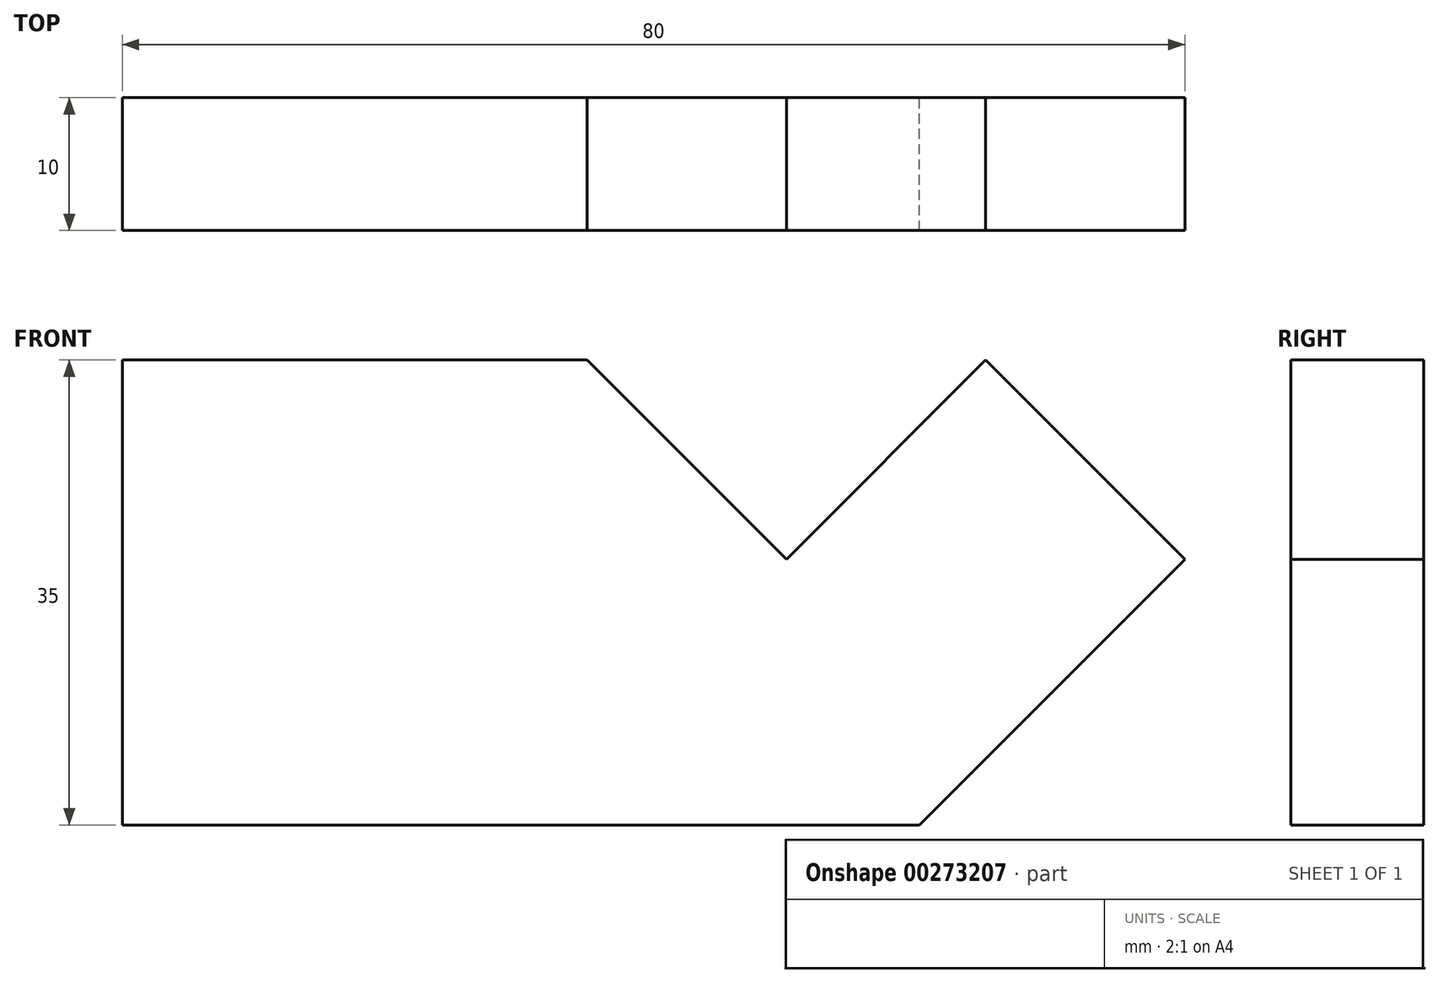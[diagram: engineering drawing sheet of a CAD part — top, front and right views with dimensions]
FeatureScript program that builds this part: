
annotation { "Feature Type Name" : "Feature", "Feature Type Description" : "" }
export const myFeature = defineFeature(function(context is Context, id is Id, definition is map)
    precondition{}
    {
        {
            var Q0;
            Q0=qCreatedBy(makeId("Front.planeOp"),FACE);
            var sketch = newSketch(context, id + "F0", { "sketchPlane" : qUnion([Q0])});
            skLineSegment(sketch, "E0", {"start": v(0, 0) * mm, "end": v(0, 35) * mm});
            skLineSegment(sketch, "E1", {"start": v(0, 0) * mm, "end": v(60, 0) * mm});
            skLineSegment(sketch, "E2", {"start": v(60, 0) * mm, "end": v(80, 20) * mm});
            skLineSegment(sketch, "E3", {"start": v(0, 35) * mm, "end": v(35, 35) * mm});
            skLineSegment(sketch, "E4", {"start": v(35, 35) * mm, "end": v(50, 20) * mm});
            skLineSegment(sketch, "E5", {"start": v(65, 35) * mm, "end": v(80, 20) * mm});
            skLineSegment(sketch, "E6", {"start": v(50, 20) * mm, "end": v(65, 35) * mm});
            skSolve(sketch);
        }
        {
            var Q0;
            Q0 = qSketchRegion(id + "F0", true);
            extrude(context, id + "F1", {"entities" : qUnion([Q0]), "depth" : 10 * mm});
        }
    });
